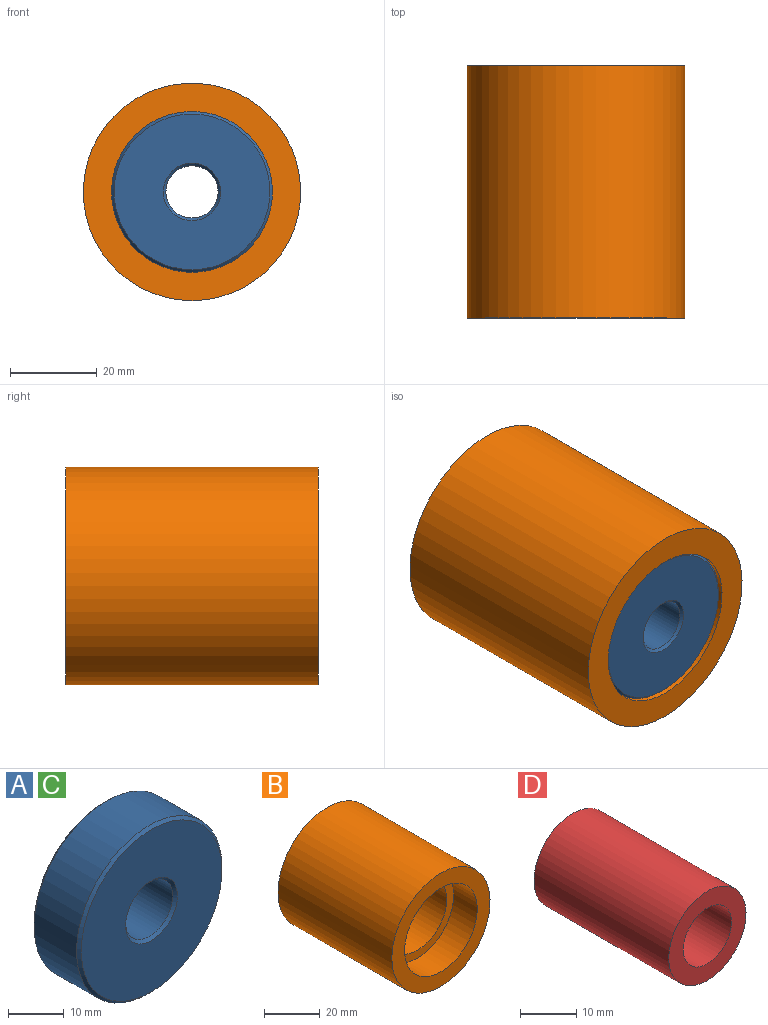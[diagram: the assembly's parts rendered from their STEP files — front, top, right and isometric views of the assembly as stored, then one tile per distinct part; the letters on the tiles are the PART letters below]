
ASSEMBLY  parts=4 mates=3
PART A: 8 faces, bbox 37x12x37 mm
  f0: cylinder r=18.5mm len=37mm, axis (0,1,0), area 1255.4mm2, adj f4,f5
  f1: cylinder r=6mm len=12mm, axis (0,1,0), area 407.2mm2, adj f6,f7
  f2: plane 35.8x35.8mm, normal (0,-1,0), area 869.7mm2, adj f4,f7
  f3: plane 35.8x35.8mm, normal (0,1,0), area 869.7mm2, adj f5,f6
  f4: cone r=17.9mm half-angle=45deg, axis (0,1,0), area 97mm2, adj f0,f2
  f5: cone r=18.5mm half-angle=45deg, axis (0,-1,0), area 97mm2, adj f0,f3
  f6: cone r=6.6mm half-angle=45deg, axis (0,1,0), area 33.6mm2, adj f1,f3
  f7: cone r=6mm half-angle=45deg, axis (0,-1,0), area 33.6mm2, adj f1,f2
PART B: 8 faces, bbox 50x58x50 mm
  f0: cylinder r=18.5mm len=37mm, axis (0,1,0), area 1394.9mm2, adj f4,f7
  f1: cylinder r=18.5mm len=37mm, axis (0,1,0), area 1394.9mm2, adj f3,f6
  f2: cylinder r=25mm len=58mm, axis (0,1,0), area 9110.6mm2, adj f3,f4
  f3: plane 50x50mm, normal (0,-1,0), area 888.3mm2, adj f1,f2
  f4: plane 50x50mm, normal (0,1,0), area 888.3mm2, adj f0,f2
  f5: cylinder r=15mm len=34mm, axis (0,1,0), area 3204.4mm2, adj f6,f7
  f6: plane 37x37mm, normal (0,-1,0), area 368.4mm2, adj f1,f5
  f7: plane 37x37mm, normal (0,1,0), area 368.4mm2, adj f0,f5
PART C: same geometry as A
PART D: 4 faces, bbox 19.5x34x19.5 mm
  f0: cylinder r=6.1mm len=34mm, axis (0,1,0), area 1303.1mm2, adj f2,f3
  f1: cylinder r=9.75mm len=34mm, axis (0,1,0), area 2082.9mm2, adj f2,f3
  f2: plane 19.5x19.5mm, normal (0,-1,0), area 181.7mm2, adj f0,f1
  f3: plane 19.5x19.5mm, normal (0,1,0), area 181.7mm2, adj f0,f1
PLACE A t=(-24.54,-22.31,12.4)mm
PLACE B t=(-24.54,-5.91,12.4)mm
PLACE C t=(-24.54,22.49,12.4)mm
PLACE D t=(-24.54,11.09,12.4)mm
MATE fastened A.f1 <-> B.f5  axis (0,1,0) through (-24.54,-22.91,12.4)mm
MATE fastened D.f0 <-> B.f5  axis (0,1,0) through (-24.54,11.09,12.4)mm
MATE fastened C.f1 <-> B.f5  axis (0,-1,0) through (-24.54,11.09,12.4)mm
